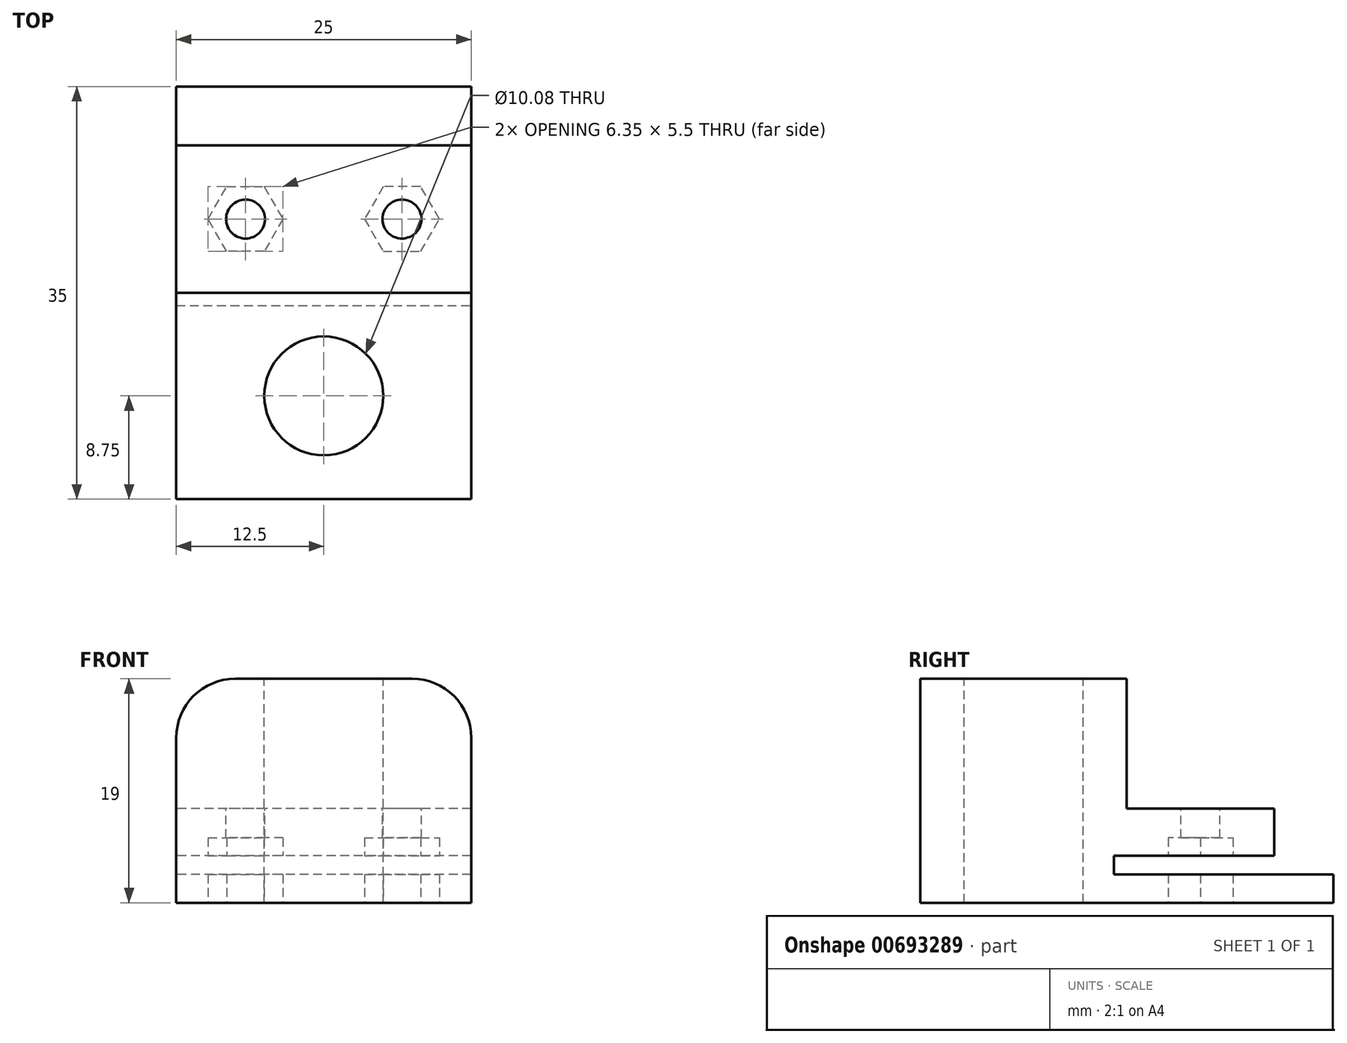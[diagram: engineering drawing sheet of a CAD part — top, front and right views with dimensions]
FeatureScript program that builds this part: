
annotation { "Feature Type Name" : "Feature", "Feature Type Description" : "" }
export const myFeature = defineFeature(function(context is Context, id is Id, definition is map)
    precondition{}
    {
        {
            var Q0;
            Q0=qCreatedBy(makeId("Top.planeOp"),FACE);
            var sketch = newSketch(context, id + "F0", { "sketchPlane" : qUnion([Q0])});
            skLineSegment(sketch, "E0.bottom", {"start": v(12.5, 17.5) * mm, "end": v(-12.5, 17.5) * mm});
            skLineSegment(sketch, "E0.top", {"start": v(12.5, -17.5) * mm, "end": v(-12.5, -17.5) * mm});
            skLineSegment(sketch, "E0.left", {"start": v(12.5, 17.5) * mm, "end": v(12.5, -17.5) * mm});
            skLineSegment(sketch, "E0.right", {"start": v(-12.5, 17.5) * mm, "end": v(-12.5, -17.5) * mm});
            skPoint(sketch, "E0.middle", {"position": v(0, 0) * mm});
            skLineSegment(sketch, "E1", {"start": v(-35.58, 0.02) * mm, "end": v(34.42, 0.02) * mm, "construction": true});
            skSolve(sketch);
        }
        {
            var Q0;
            Q0=qSketchRegion(id+"F0",true);
            extrude(context, id + "F1", {"entities" : qUnion([Q0]), "depth" : 4 * mm, "offsetDistance" : 25 * mm});
        }
        {
            var Q0;
            Q0=makeQuery(id+"F1.opExtrude","CAP_FACE",FACE,{"disambiguationData":[OSD([sQuery(id+"F0.wireOp",EDGE,"E0.bottom"),sQuery(id+"F0.wireOp",EDGE,"E0.top"),sQuery(id+"F0.wireOp",EDGE,"E0.left"),sQuery(id+"F0.wireOp",EDGE,"E0.right")])],"isStart":false});
            var sketch = newSketch(context, id + "F2", { "sketchPlane" : qUnion([Q0])});
            skLineSegment(sketch, "E2.bottom", {"start": v(12.5, 12.5) * mm, "end": v(-12.5, 12.5) * mm});
            skLineSegment(sketch, "E2.top", {"start": v(12.5, -12.5) * mm, "end": v(-12.5, -12.5) * mm});
            skLineSegment(sketch, "E2.left", {"start": v(12.5, 12.5) * mm, "end": v(12.5, -12.5) * mm});
            skLineSegment(sketch, "E2.right", {"start": v(-12.5, 12.5) * mm, "end": v(-12.5, -12.5) * mm});
            skPoint(sketch, "E2.middle", {"position": v(0, 0) * mm});
            skSolve(sketch);
        }
        {
            var Q0;
            {var subQ0=sQuery(id+"F2.wireOp",EDGE,"E2.left");var subQ1=makeQuery(id+"F1.opExtrude","CAP_EDGE",EDGE,{"disambiguationData":[OSD([sQuery(id+"F0.wireOp",EDGE,"E0.bottom")])],"isStart":false});var subQ2=makeQuery(id+"F2.imprint","INTERSECT",VERTEX,{"derivedFrom":[subQ1,subQ0]});Q0=makeQuery(id+"F2.imprint","IMPRINT",FACE,{"disambiguationData":[TD([[makeQuery(id+"F2.imprint","IMPRINT",EDGE,{"disambiguationData":[TD([[subQ2,-1.0]])],"derivedFrom":subQ0}),-1.0]])]});}
            var Q1;
            {var subQ0=sQuery(id+"F2.wireOp",EDGE,"E2.top");Q1=makeQuery(id+"F2.imprint","IMPRINT",FACE,{"disambiguationData":[TD([[makeQuery(id+"F2.imprint","IMPRINT",EDGE,{"derivedFrom":subQ0}),1.0]])]});}
            extrude(context, id + "F3", {"entities" : qUnion([Q0, Q1]), "operationType" : NewBodyOperationType.ADD, "depth" : 15 * mm, "offsetDistance" : 25 * mm});
        }
        {
            var Q0;
            Q0=makeQuery(id+"F3.opExtrude","CAP_EDGE",EDGE,{"disambiguationData":[OSD([sQuery(id+"F2.wireOp",EDGE,"E2.right")])],"isStart":true});
            var Q1;
            Q1=makeQuery(id+"F3.opExtrude","CAP_EDGE",EDGE,{"disambiguationData":[OSD([sQuery(id+"F2.wireOp",EDGE,"E2.right")])],"isStart":false});
            var Q2;
            Q2=makeQuery(id+"F3.opExtrude","CAP_EDGE",EDGE,{"disambiguationData":[OSD([sQuery(id+"F2.wireOp",EDGE,"E2.left")])],"isStart":false});
            var Q3;
            Q3=makeQuery(id+"F3.opExtrude","CAP_EDGE",EDGE,{"disambiguationData":[OSD([sQuery(id+"F2.wireOp",EDGE,"E2.left")])],"isStart":true});
            fillet(context, id + "F4", {"entities" : qUnion([Q0, Q1, Q2, Q3]), "radius" : 5 * mm, "tangentPropagation" : true, "allowEdgeOverflow" : false});
        }
        {
            var Q0;
            Q0=makeQuery(id+"F3.opExtrude","CAP_FACE",FACE,{"disambiguationData":[OSD([sQuery(id+"F2.wireOp",EDGE,"E2.bottom"),sQuery(id+"F2.wireOp",EDGE,"E2.top"),sQuery(id+"F2.wireOp",EDGE,"E2.left"),sQuery(id+"F2.wireOp",EDGE,"E2.right")])],"isStart":false});
            var sketch = newSketch(context, id + "F5", { "sketchPlane" : qUnion([Q0])});
            skLineSegment(sketch, "E3", {"start": v(-16.38, 0) * mm, "end": v(18.29, 0) * mm});
            skLineSegment(sketch, "E4", {"start": v(18.29, 0) * mm, "end": v(18.29, 17.63) * mm});
            skLineSegment(sketch, "E5", {"start": v(18.29, 17.63) * mm, "end": v(-16.38, 17.63) * mm});
            skLineSegment(sketch, "E6", {"start": v(-16.38, 17.63) * mm, "end": v(-16.38, 0) * mm});
            skSolve(sketch);
        }
        {
            var Q0;
            {var subQ0=sQuery(id+"F5.wireOp",EDGE,"E4");Q0=makeQuery(id+"F5.imprint","IMPRINT",FACE,{"disambiguationData":[TD([[makeQuery(id+"F5.imprint","IMPRINT",EDGE,{"derivedFrom":subQ0}),1.0]])]});}
            var Q1;
            {var subQ3=sQuery(id+"F2.wireOp",EDGE,"E2.bottom");var subQ9=makeQuery(id+"F3.opExtrude","CAP_EDGE",EDGE,{"disambiguationData":[OSD([subQ3])],"isStart":false});Q1=makeQuery(id+"F5.imprint","IMPRINT",FACE,{"disambiguationData":[TD([[makeQuery(id+"F5.imprint","IMPRINT",EDGE,{"derivedFrom":subQ9}),1.0]])]});}
            extrude(context, id + "F6", {"entities" : qUnion([Q0, Q1]), "operationType" : NewBodyOperationType.REMOVE, "oppositeDirection" : true, "depth" : 11 * mm, "offsetDistance" : 25 * mm});
        }
        {
            var Q0;
            Q0=makeQuery(id+"F3.boolean.opBoolean","MERGE",FACE,{"derivedFrom":[makeQuery(id+"F1.opExtrude","SWEPT_FACE",FACE,{"disambiguationData":[OSD([sQuery(id+"F0.wireOp",EDGE,"E0.left")])]}),makeQuery(id+"F3.opExtrude","SWEPT_FACE",FACE,{"disambiguationData":[OSD([sQuery(id+"F2.wireOp",EDGE,"E2.left")])]})]});
            var sketch = newSketch(context, id + "F7", { "sketchPlane" : qUnion([Q0])});
            skLineSegment(sketch, "E7.bottom", {"start": v(18.9, 4) * mm, "end": v(-1.1, 4) * mm});
            skLineSegment(sketch, "E7.top", {"start": v(18.9, 2.4) * mm, "end": v(-1.1, 2.4) * mm});
            skLineSegment(sketch, "E7.left", {"start": v(18.9, 4) * mm, "end": v(18.9, 2.4) * mm});
            skLineSegment(sketch, "E7.right", {"start": v(-1.1, 4) * mm, "end": v(-1.1, 2.4) * mm});
            skSolve(sketch);
        }
        {
            var Q0;
            Q0=makeQuery(id+"F6.boolean.opBoolean","COPY",FACE,{"derivedFrom":makeQuery(id+"F6.opExtrude","CAP_FACE",FACE,{"disambiguationData":[OSD([sQuery(id+"F5.wireOp",EDGE,"E3"),sQuery(id+"F5.wireOp",EDGE,"E4"),sQuery(id+"F5.wireOp",EDGE,"E5"),sQuery(id+"F5.wireOp",EDGE,"E6")])],"isStart":false})});
            var sketch = newSketch(context, id + "F8", { "sketchPlane" : qUnion([Q0])});
            skPoint(sketch, "E8", {"position": v(6.63, 6.25) * mm});
            skPoint(sketch, "E8.positionSnap0", {"position": v(12.5, 6.25) * mm});
            skPoint(sketch, "E9.MirrorP", {"position": v(-6.63, 6.25) * mm});
            skSolve(sketch);
        }
        {
            var Q0;
            Q0=sQuery(id+"F8.wireOp",VERTEX,"E8");
            var Q1;
            Q1=sQuery(id+"F8.wireOp",VERTEX,"E9.MirrorP");
            var Q2;
            Q2=makeQuery(id+"F1.opExtrude","SWEPT_BODY",BODY,{"disambiguationData":[OSD([sQuery(id+"F0.wireOp",EDGE,"E0.bottom"),sQuery(id+"F0.wireOp",EDGE,"E0.top"),sQuery(id+"F0.wireOp",EDGE,"E0.left"),sQuery(id+"F0.wireOp",EDGE,"E0.right")])]});
            hole(context, id + "F9", {"style" : HoleStyle.SIMPLE, "endStyle" : HoleEndStyle.THROUGH, "standardTappedOrClearance" : lookupTablePath({ "standard" : "ISO", "fit" : "Normal", "size" : "M3", "type" : "Clearance" }), "standardBlindInLast" : lookupTablePath({ "fit" : "Standard", "standard" : "ISO", "size" : "M3", "type" : "Clearance" }), "holeDiameter" : 3.3 * mm, "majorDiameter" : 5 * mm, "isTappedThrough" : true, "tappedDepth" : 12 * mm, "tapClearance" : 3, "startFromSketch" : true, "locations" : qUnion([Q0, Q1]), "scope" : qUnion([Q2])});
        }
        {
            var Q0;
            Q0=makeQuery(id+"F0.imprint","IMPRINT",FACE,{"disambiguationData":[TD([[makeQuery(id+"F0.imprint","IMPRINT",EDGE,{"derivedFrom":sQuery(id+"F0.wireOp",EDGE,"E0.bottom")}),1.0]])]});
            var sketch = newSketch(context, id + "F10", { "sketchPlane" : qUnion([Q0])});
            skCircle(sketch, "E10.cCircle", {"center": v(-6.63, 6.25) * mm, "radius": 2.75 * mm, "construction": true});
            skLineSegment(sketch, "E10.0", {"start": v(-3.45, 6.25) * mm, "end": v(-5.04, 3.5) * mm});
            skLineSegment(sketch, "E10.1", {"start": v(-5.04, 3.5) * mm, "end": v(-8.22, 3.5) * mm});
            skLineSegment(sketch, "E10.2", {"start": v(-8.22, 3.5) * mm, "end": v(-9.8, 6.25) * mm});
            skLineSegment(sketch, "E10.3", {"start": v(-9.8, 6.25) * mm, "end": v(-8.22, 9) * mm});
            skLineSegment(sketch, "E10.4", {"start": v(-8.22, 9) * mm, "end": v(-5.04, 9) * mm});
            skLineSegment(sketch, "E10.5", {"start": v(-5.04, 9) * mm, "end": v(-3.45, 6.25) * mm});
            skPoint(sketch, "E10.0.midPoint", {"position": v(-4.25, 4.87) * mm});
            skLineSegment(sketch, "E11.MirrorCS", {"start": v(3.45, 6.25) * mm, "end": v(5.04, 3.5) * mm});
            skLineSegment(sketch, "E12.MirrorCS", {"start": v(9.8, 6.25) * mm, "end": v(8.22, 9) * mm});
            skPoint(sketch, "E13.MirrorP", {"position": v(4.25, 4.87) * mm});
            skCircle(sketch, "E14.MirrorC", {"center": v(6.63, 6.25) * mm, "radius": 2.75 * mm, "construction": true});
            skLineSegment(sketch, "E15.MirrorCS", {"start": v(5.04, 3.5) * mm, "end": v(8.22, 3.5) * mm});
            skLineSegment(sketch, "E16.MirrorCS", {"start": v(8.22, 3.5) * mm, "end": v(9.8, 6.25) * mm});
            skLineSegment(sketch, "E17.MirrorCS", {"start": v(8.22, 9) * mm, "end": v(5.04, 9) * mm});
            skLineSegment(sketch, "E18.MirrorCS", {"start": v(5.04, 9) * mm, "end": v(3.45, 6.25) * mm});
            skSolve(sketch);
        }
        {
            var Q0;
            Q0 = qSketchRegion(id + "F10", true);
            extrude(context, id + "F11", {"entities" : qUnion([Q0]), "operationType" : NewBodyOperationType.REMOVE, "depth" : 5.5 * mm, "offsetDistance" : 25 * mm});
        }
        {
            var Q0;
            Q0 = qSketchRegion(id + "F7", true);
            extrude(context, id + "F12", {"entities" : qUnion([Q0]), "operationType" : NewBodyOperationType.REMOVE, "oppositeDirection" : true, "depth" : 25 * mm, "offsetDistance" : 25 * mm});
        }
        {
            var Q0;
            Q0=makeQuery(id+"F3.opExtrude","CAP_FACE",FACE,{"disambiguationData":[OSD([sQuery(id+"F0.wireOp",EDGE,"E0.top"),sQuery(id+"F0.wireOp",EDGE,"E0.left"),sQuery(id+"F0.wireOp",EDGE,"E0.right"),sQuery(id+"F2.wireOp",EDGE,"E2.bottom"),sQuery(id+"F2.wireOp",EDGE,"E2.left"),sQuery(id+"F2.wireOp",EDGE,"E2.right")])],"isStart":false});
            var sketch = newSketch(context, id + "F13", { "sketchPlane" : qUnion([Q0])});
            skPoint(sketch, "E19", {"position": v(0, -8.75) * mm});
            skPoint(sketch, "E19.positionSnap0", {"position": v(0, -17.5) * mm});
            skPoint(sketch, "E19.positionSnap1", {"position": v(-7.5, -8.75) * mm});
            skSolve(sketch);
        }
        {
            var Q0;
            Q0=sQuery(id+"F13.wireOp",VERTEX,"E19");
            var Q1;
            Q1=makeQuery(id+"F1.opExtrude","SWEPT_BODY",BODY,{"disambiguationData":[OSD([sQuery(id+"F0.wireOp",EDGE,"E0.bottom"),sQuery(id+"F0.wireOp",EDGE,"E0.top"),sQuery(id+"F0.wireOp",EDGE,"E0.left"),sQuery(id+"F0.wireOp",EDGE,"E0.right")])]});
            hole(context, id + "F14", {"style" : HoleStyle.SIMPLE, "endStyle" : HoleEndStyle.THROUGH, "standardTappedOrClearance" : lookupTablePath({ "standard" : "ANSI", "fit" : "Normal (ASME)", "size" : "3/8", "type" : "Clearance" }), "standardBlindInLast" : lookupTablePath({ "fit" : "Free", "standard" : "ANSI", "size" : "3/8", "type" : "Clearance" }), "holeDiameter" : 10.08 * mm, "majorDiameter" : 5 * mm, "isTappedThrough" : true, "tappedDepth" : 12 * mm, "tapClearance" : 3, "startFromSketch" : true, "locations" : qUnion([Q0]), "scope" : qUnion([Q1])});
        }
    });
